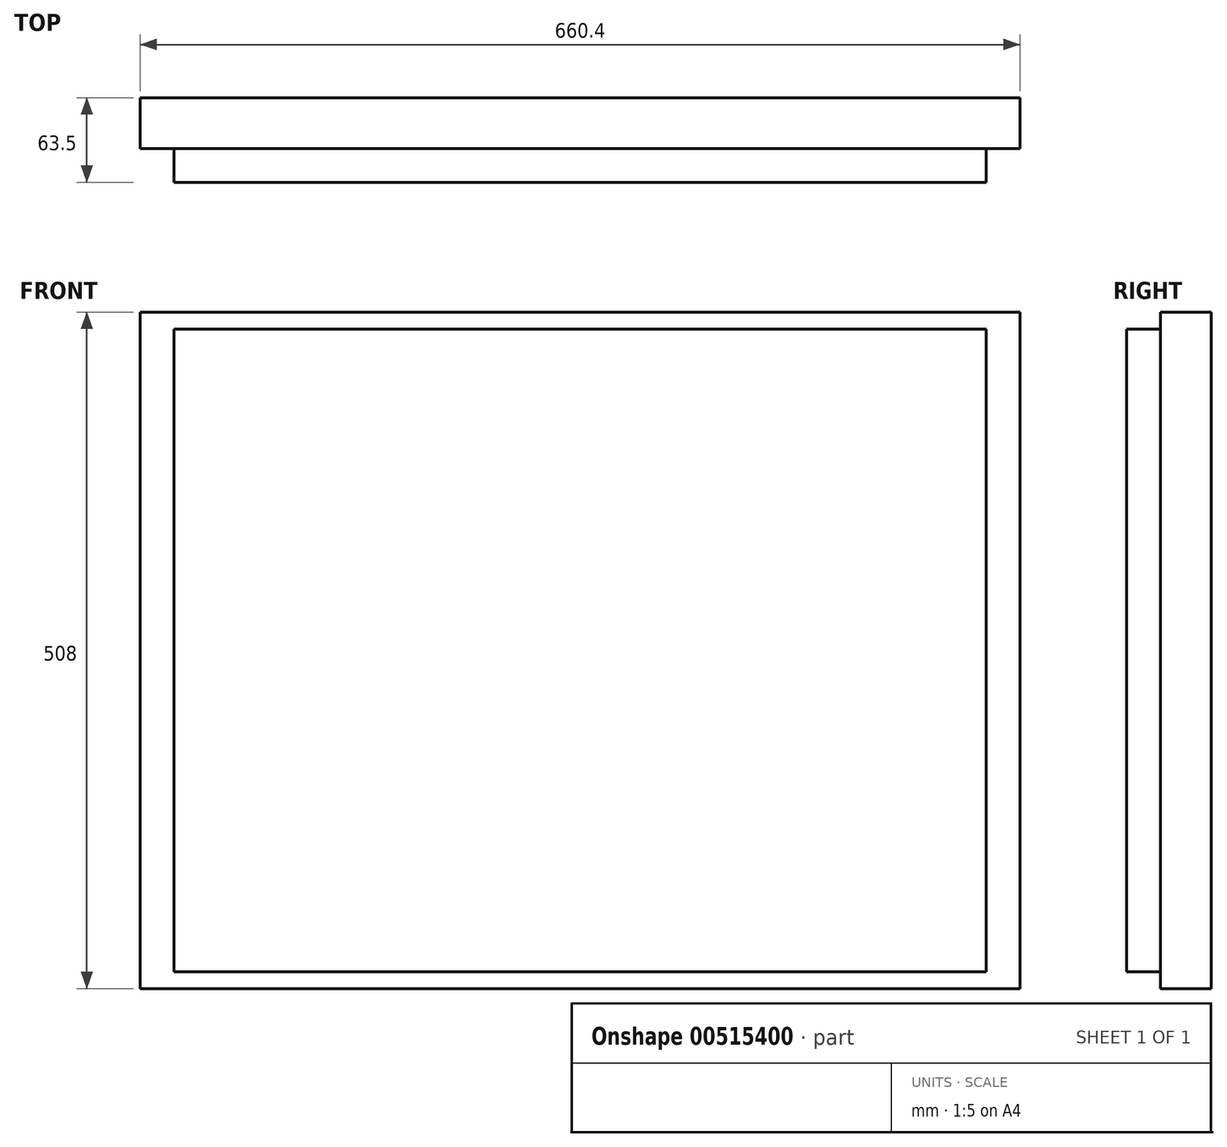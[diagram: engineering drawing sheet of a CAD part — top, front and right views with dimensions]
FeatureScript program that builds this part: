
annotation { "Feature Type Name" : "Feature", "Feature Type Description" : "" }
export const myFeature = defineFeature(function(context is Context, id is Id, definition is map)
    precondition{}
    {
        {
            var Q0;
            Q0=qCreatedBy(makeId("Front.planeOp"),FACE);
            var sketch = newSketch(context, id + "F0", { "sketchPlane" : qUnion([Q0])});
            skLineSegment(sketch, "E0.bottom", {"start": v(0, 0) * mm, "end": v(-660.4, 0) * mm});
            skLineSegment(sketch, "E0.top", {"start": v(0, 508) * mm, "end": v(-660.4, 508) * mm});
            skLineSegment(sketch, "E0.left", {"start": v(0, 0) * mm, "end": v(0, 508) * mm});
            skLineSegment(sketch, "E0.right", {"start": v(-660.4, 0) * mm, "end": v(-660.4, 508) * mm});
            skSolve(sketch);
        }
        {
            var Q0;
            Q0=makeQuery(id+"F0.imprint","IMPRINT",FACE,{"disambiguationData":[TD([[makeQuery(id+"F0.imprint","IMPRINT",EDGE,{"derivedFrom":sQuery(id+"F0.wireOp",EDGE,"E0.bottom")}),-1.0]])]});
            extrude(context, id + "F1", {"entities" : qUnion([Q0]), "depth" : 38.1 * mm, "offsetDistance" : 25.4 * mm});
        }
        {
            var Q0;
            Q0=makeQuery(id+"F1.opExtrude","CAP_FACE",FACE,{"disambiguationData":[OSD([sQuery(id+"F0.wireOp",EDGE,"E0.bottom"),sQuery(id+"F0.wireOp",EDGE,"E0.top"),sQuery(id+"F0.wireOp",EDGE,"E0.left"),sQuery(id+"F0.wireOp",EDGE,"E0.right")])],"isStart":false});
            var sketch = newSketch(context, id + "F2", { "sketchPlane" : qUnion([Q0])});
            skLineSegment(sketch, "E1", {"start": v(-660.4, 0) * mm, "end": v(-635, 0) * mm});
            skLineSegment(sketch, "E2", {"start": v(-635, 0) * mm, "end": v(-635, 12.7) * mm});
            skLineSegment(sketch, "E3", {"start": v(0, 508) * mm, "end": v(-25.4, 508) * mm});
            skLineSegment(sketch, "E4", {"start": v(-25.4, 508) * mm, "end": v(-25.4, 495.3) * mm});
            skLineSegment(sketch, "E5.bottom", {"start": v(-635, 12.7) * mm, "end": v(-25.4, 12.7) * mm});
            skLineSegment(sketch, "E5.top", {"start": v(-635, 495.3) * mm, "end": v(-25.4, 495.3) * mm});
            skLineSegment(sketch, "E5.left", {"start": v(-635, 12.7) * mm, "end": v(-635, 495.3) * mm});
            skLineSegment(sketch, "E5.right", {"start": v(-25.4, 12.7) * mm, "end": v(-25.4, 495.3) * mm});
            skSolve(sketch);
        }
        {
            var Q0;
            Q0=makeQuery(id+"F2.imprint","IMPRINT",FACE,{"disambiguationData":[TD([[makeQuery(id+"F2.imprint","IMPRINT",EDGE,{"derivedFrom":sQuery(id+"F2.wireOp",EDGE,"E5.bottom")}),1.0]])]});
            extrude(context, id + "F3", {"entities" : qUnion([Q0]), "operationType" : NewBodyOperationType.ADD, "depth" : 25.4 * mm, "offsetDistance" : 25.4 * mm});
        }
    });
